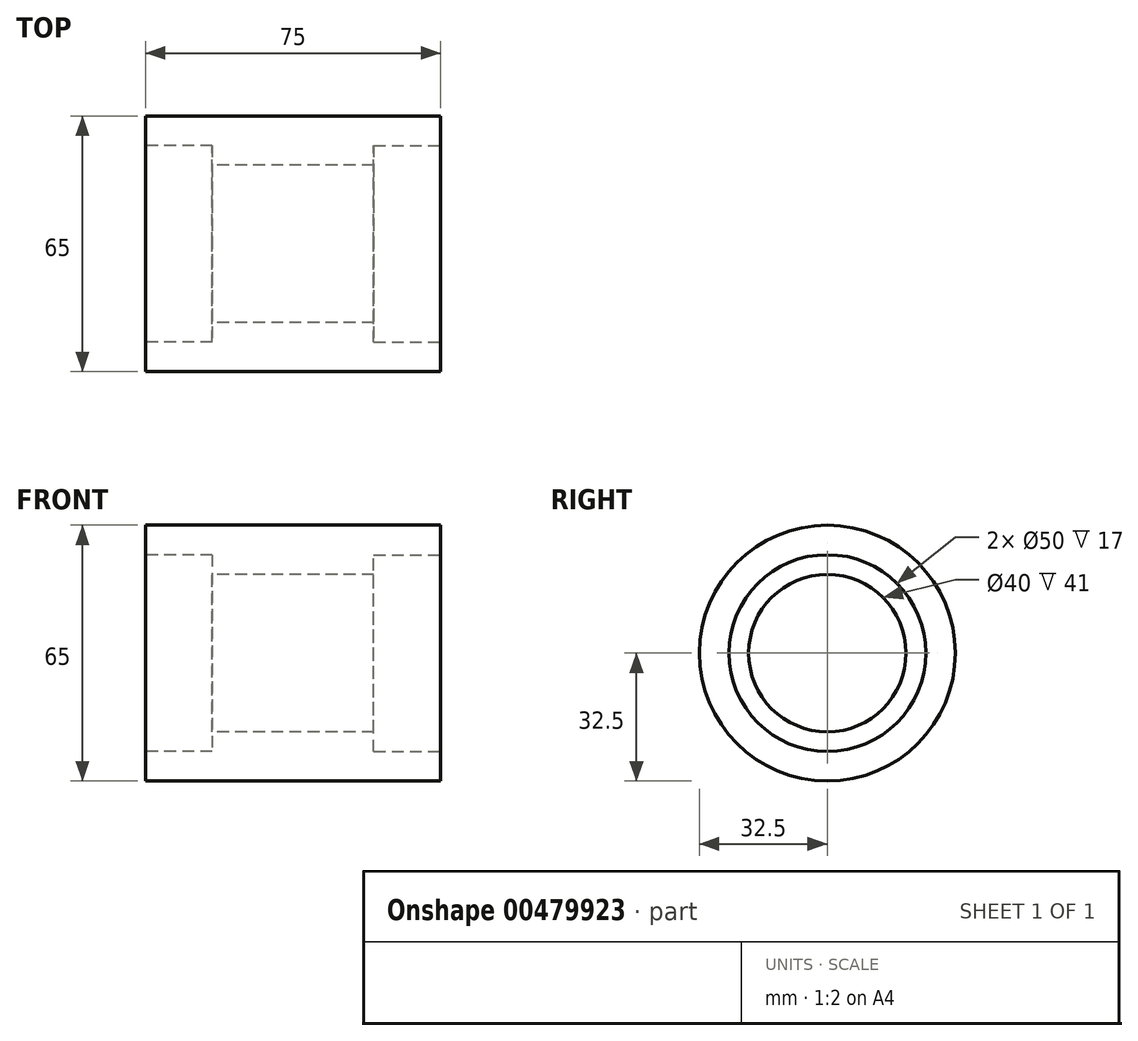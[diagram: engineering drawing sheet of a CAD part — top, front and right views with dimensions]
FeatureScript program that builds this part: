
annotation { "Feature Type Name" : "Feature", "Feature Type Description" : "" }
export const myFeature = defineFeature(function(context is Context, id is Id, definition is map)
    precondition{}
    {
        {
            var Q0;
            Q0=qCreatedBy(makeId("Right.planeOp"),FACE);
            var sketch = newSketch(context, id + "F0", { "sketchPlane" : qUnion([Q0])});
            skCircle(sketch, "E0", {"center": v(0, 0) * mm, "radius": 32.5 * mm});
            skCircle(sketch, "E1", {"center": v(0, 0) * mm, "radius": 20 * mm});
            skSolve(sketch);
        }
        {
            var Q0;
            Q0=makeQuery(id+"F0.imprint","IMPRINT",FACE,{"disambiguationData":[TD([[makeQuery(id+"F0.imprint","IMPRINT",EDGE,{"derivedFrom":sQuery(id+"F0.wireOp",EDGE,"E0")}),1.0]])]});
            extrude(context, id + "F1", {"entities" : qUnion([Q0]), "endBound" : BoundingType.SYMMETRIC, "depth" : 75 * mm});
        }
        {
            var Q0;
            Q0=makeQuery(id+"F1.opExtrude","CAP_FACE",FACE,{"disambiguationData":[OSD([sQuery(id+"F0.wireOp",EDGE,"E0"),sQuery(id+"F0.wireOp",EDGE,"E1")])],"isStart":false});
            var sketch = newSketch(context, id + "F2", { "sketchPlane" : qUnion([Q0])});
            skCircle(sketch, "E2.0", {"center": v(0, 0) * mm, "radius": 25 * mm});
            skSolve(sketch);
        }
        {
            var Q0;
            Q0=makeQuery(id+"F2.imprint","IMPRINT",FACE,{"disambiguationData":[TD([[makeQuery(id+"F2.imprint","IMPRINT",EDGE,{"derivedFrom":sQuery(id+"F2.wireOp",EDGE,"E2.0")}),1.0]])]});
            extrude(context, id + "F3", {"entities" : qUnion([Q0]), "operationType" : NewBodyOperationType.REMOVE, "oppositeDirection" : true, "depth" : 17 * mm});
        }
        {
            var Q0;
            Q0=makeQuery(id+"F1.opExtrude","CAP_FACE",FACE,{"disambiguationData":[OSD([sQuery(id+"F0.wireOp",EDGE,"E0"),sQuery(id+"F0.wireOp",EDGE,"E1")])],"isStart":true});
            var sketch = newSketch(context, id + "F4", { "sketchPlane" : qUnion([Q0])});
            skCircle(sketch, "E3.0", {"center": v(0, 0) * mm, "radius": 25 * mm});
            skSolve(sketch);
        }
        {
            var Q0;
            Q0=makeQuery(id+"F4.imprint","IMPRINT",FACE,{"disambiguationData":[TD([[makeQuery(id+"F4.imprint","IMPRINT",EDGE,{"derivedFrom":sQuery(id+"F4.wireOp",EDGE,"E3.0")}),1.0]])]});
            extrude(context, id + "F5", {"entities" : qUnion([Q0]), "operationType" : NewBodyOperationType.REMOVE, "oppositeDirection" : true, "depth" : 17 * mm});
        }
    });
